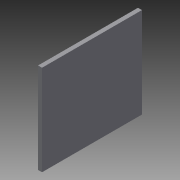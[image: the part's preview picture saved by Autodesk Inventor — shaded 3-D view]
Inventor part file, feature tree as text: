
AUTODESK INVENTOR PART (.ipt)
format: ipt  version: 2013 (Build 170138000, 138)  size: 65,536 bytes
history: native  units: mm
features: extrude x1, sketch x1
ambient origin geometry x8: Origin, YZ Plane, XZ Plane, XY Plane, X Axis, Y Axis, Z Axis, Center Point
bodies: Solid1 (feature_tree)
feature tree (2):
  extrude  "Extrusion1"  Depth=500.0mm
  sketch  "Sketch1"  dims[d0=552.0mm d2=500.0mm d3=22.0mm d4=0.0mm]
